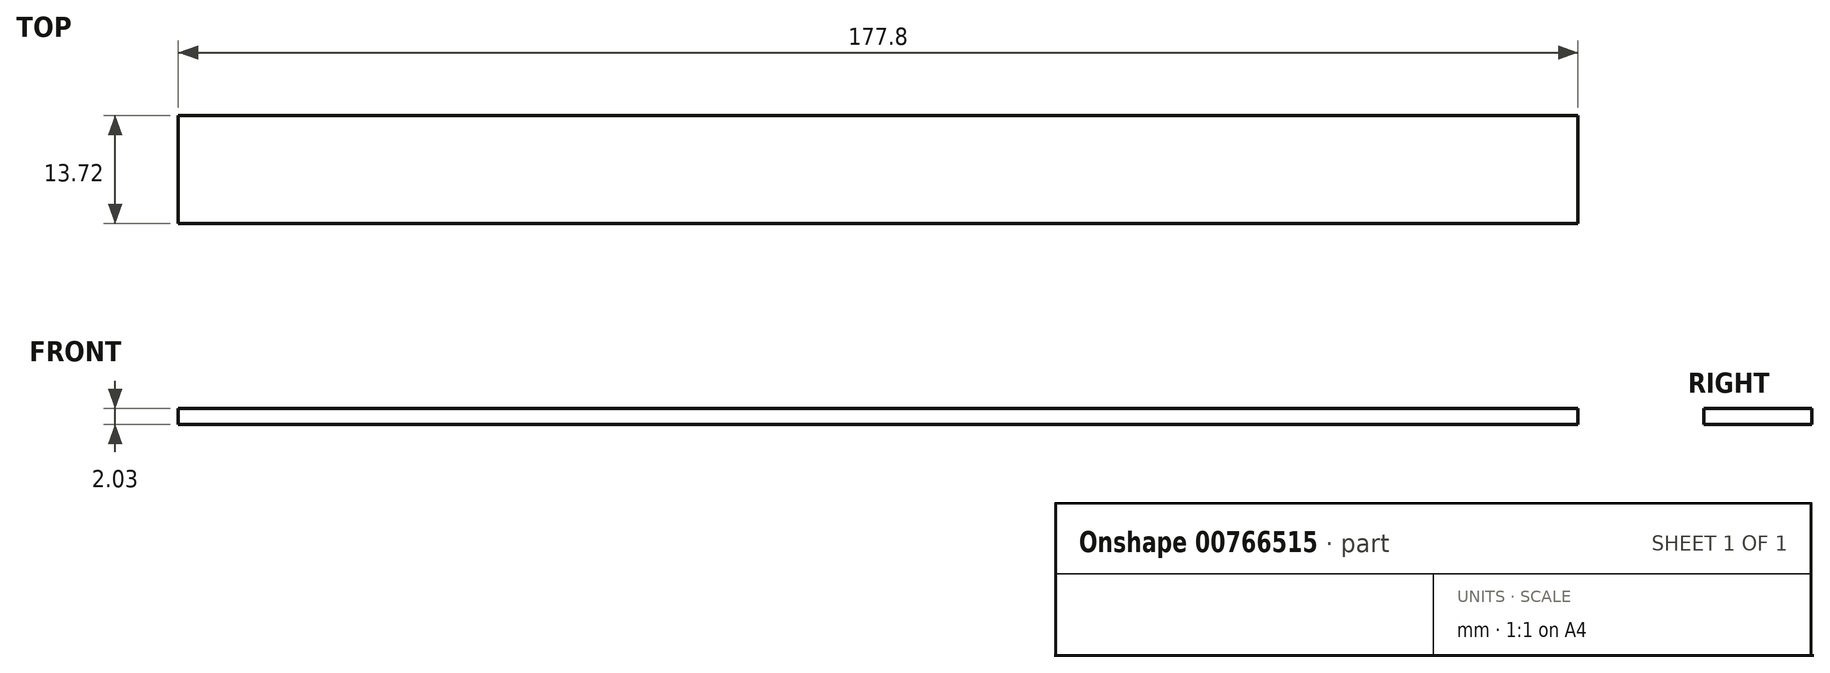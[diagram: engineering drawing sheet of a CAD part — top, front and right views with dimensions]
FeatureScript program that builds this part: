
annotation { "Feature Type Name" : "Feature", "Feature Type Description" : "" }
export const myFeature = defineFeature(function(context is Context, id is Id, definition is map)
    precondition{}
    {
        {
            var Q0;
            Q0=qCreatedBy(makeId("Top.planeOp"),FACE);
            var sketch = newSketch(context, id + "F0", { "sketchPlane" : qUnion([Q0])});
            skLineSegment(sketch, "E0.bottom", {"start": v(-88.9, 6.86) * mm, "end": v(88.9, 6.86) * mm});
            skLineSegment(sketch, "E0.top", {"start": v(-88.9, -6.86) * mm, "end": v(88.9, -6.86) * mm});
            skLineSegment(sketch, "E0.left", {"start": v(-88.9, 6.86) * mm, "end": v(-88.9, -6.86) * mm});
            skLineSegment(sketch, "E0.right", {"start": v(88.9, 6.86) * mm, "end": v(88.9, -6.86) * mm});
            skPoint(sketch, "E0.middle", {"position": v(0, 0) * mm});
            skSolve(sketch);
        }
        {
            var Q0;
            Q0=qSketchRegion(id+"F0",true);
            extrude(context, id + "F1", {"entities" : qUnion([Q0]), "depth" : 2.03 * mm, "offsetDistance" : 25.4 * mm});
        }
    });
